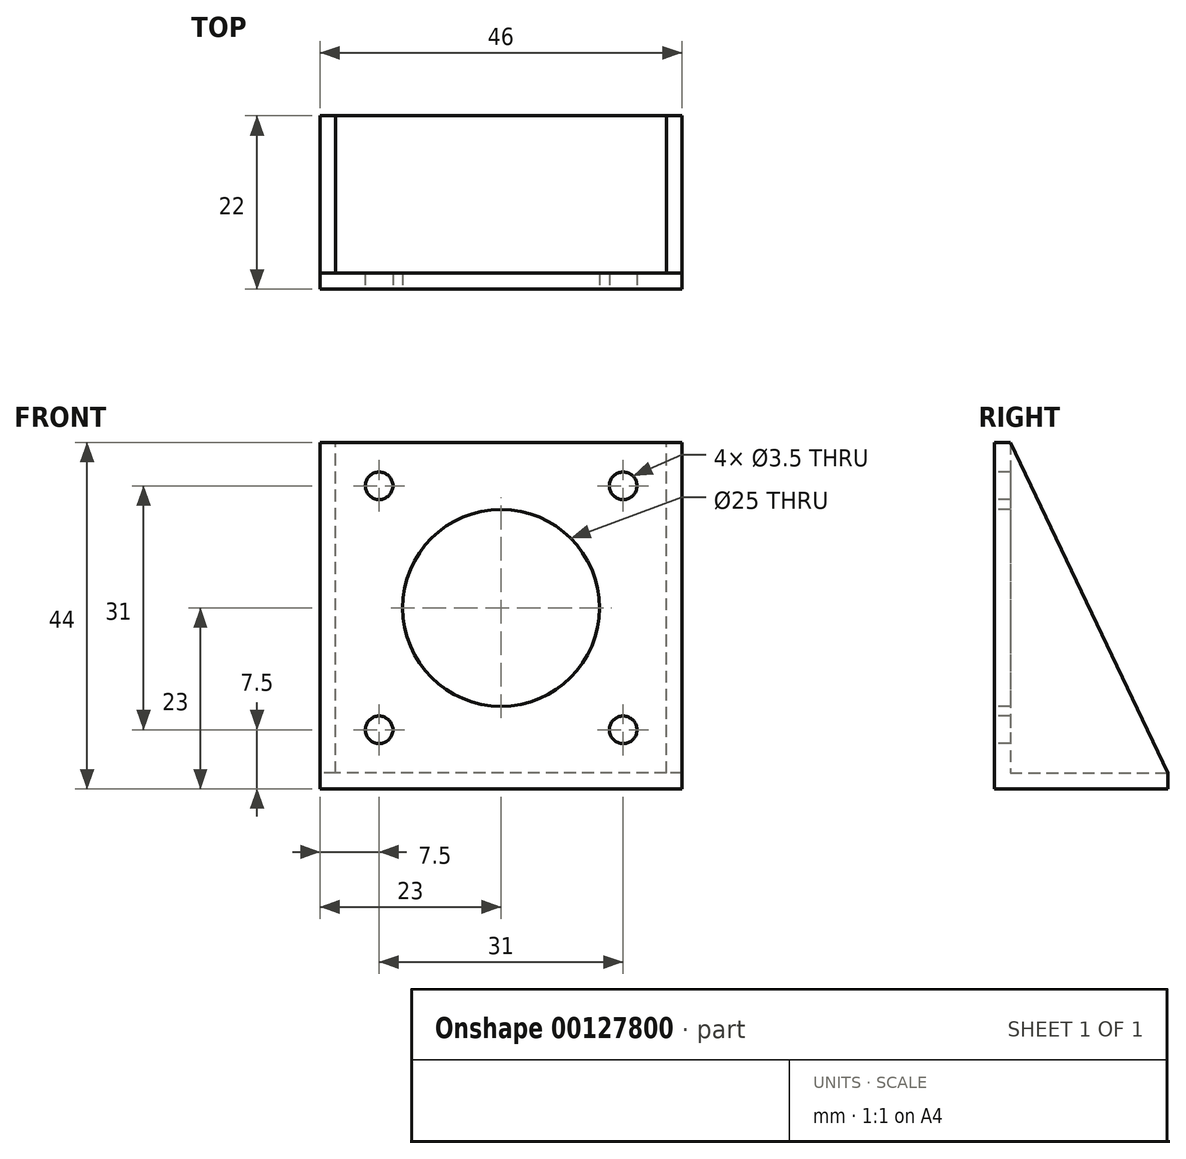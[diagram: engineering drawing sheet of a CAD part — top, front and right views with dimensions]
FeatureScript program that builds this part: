
annotation { "Feature Type Name" : "Feature", "Feature Type Description" : "" }
export const myFeature = defineFeature(function(context is Context, id is Id, definition is map)
    precondition{}
    {
        {
            var Q0;
            Q0=qCreatedBy(makeId("Right.planeOp"),FACE);
            var sketch = newSketch(context, id + "F0", { "sketchPlane" : qUnion([Q0])});
            skLineSegment(sketch, "E0", {"start": v(0, 44) * mm, "end": v(0, 0) * mm});
            skLineSegment(sketch, "E1", {"start": v(0, 0) * mm, "end": v(22, 0) * mm});
            skLineSegment(sketch, "E2", {"start": v(22, 0) * mm, "end": v(22, 2) * mm});
            skLineSegment(sketch, "E3", {"start": v(22, 2) * mm, "end": v(2, 44) * mm});
            skLineSegment(sketch, "E4", {"start": v(2, 44) * mm, "end": v(0, 44) * mm});
            skSolve(sketch);
        }
        {
            var Q0;
            Q0 = qSketchRegion(id + "F0", true);
            extrude(context, id + "F1", {"entities" : qUnion([Q0]), "endBound" : BoundingType.SYMMETRIC, "depth" : 46 * mm});
        }
        {
            var Q0;
            Q0=qCreatedBy(makeId("Right.planeOp"),FACE);
            var sketch = newSketch(context, id + "F2", { "sketchPlane" : qUnion([Q0])});
            skLineSegment(sketch, "E5", {"start": v(22, 2) * mm, "end": v(2, 44) * mm});
            skLineSegment(sketch, "E6", {"start": v(2, 44) * mm, "end": v(2, 2) * mm});
            skLineSegment(sketch, "E7", {"start": v(2, 2) * mm, "end": v(22, 2) * mm});
            skSolve(sketch);
        }
        {
            var Q0;
            Q0 = qSketchRegion(id + "F2", true);
            extrude(context, id + "F3", {"entities" : qUnion([Q0]), "operationType" : NewBodyOperationType.REMOVE, "endBound" : BoundingType.SYMMETRIC, "depth" : 42 * mm});
        }
        {
            var Q0;
            Q0=makeQuery(id+"FImADSnukrB8zGc_1.boolean.opBoolean","MERGE",FACE,{"derivedFrom":[makeQuery(id+"F1.opExtrude","SWEPT_FACE",FACE,{"disambiguationData":[OSD([sQuery(id+"F0.wireOp",EDGE,"E0")])]}),makeQuery(id+"FImADSnukrB8zGc_1.opExtrude","SWEPT_FACE",FACE,{"disambiguationData":[OSD([sQuery(id+"FoDxlGOpSHDgfe1_1.wireOp",EDGE,"XQjN4DDm-zgwg-AE0a-bWIw-GxvFoHyyYrTq.bottom")])]}),makeQuery(id+"FImADSnukrB8zGc_1.opExtrude","SWEPT_FACE",FACE,{"disambiguationData":[OSD([sQuery(id+"FoDxlGOpSHDgfe1_1.wireOp",EDGE,"502d4154-a04e-408c-9135-6015ee0be4ed3.MirrorCS")])]})]});
            var sketch = newSketch(context, id + "F4", { "sketchPlane" : qUnion([Q0])});
            skLineSegment(sketch, "E8", {"start": v(-23, 2) * mm, "end": v(23, 2) * mm, "construction": true});
            skLineSegment(sketch, "E9", {"start": v(0, 2) * mm, "end": v(0, 44) * mm, "construction": true});
            skCircle(sketch, "E10", {"center": v(0, 23) * mm, "radius": 12.5 * mm});
            skCircle(sketch, "E11", {"center": v(-15.5, 38.5) * mm, "radius": 1.75 * mm});
            skLineSegment(sketch, "E12", {"start": v(0, 23) * mm, "end": v(-46.8, 23) * mm, "construction": true});
            skCircle(sketch, "E13.MirrorC", {"center": v(-15.5, 7.5) * mm, "radius": 1.75 * mm});
            skCircle(sketch, "E14.MirrorC", {"center": v(15.5, 38.5) * mm, "radius": 1.75 * mm});
            skCircle(sketch, "E15.MirrorC", {"center": v(15.5, 7.5) * mm, "radius": 1.75 * mm});
            skSolve(sketch);
        }
        {
            var Q0;
            Q0 = qSketchRegion(id + "F4", true);
            extrude(context, id + "F5", {"entities" : qUnion([Q0]), "operationType" : NewBodyOperationType.REMOVE, "endBound" : BoundingType.THROUGH_ALL, "oppositeDirection" : true, "depth" : 25 * mm});
        }
    });
